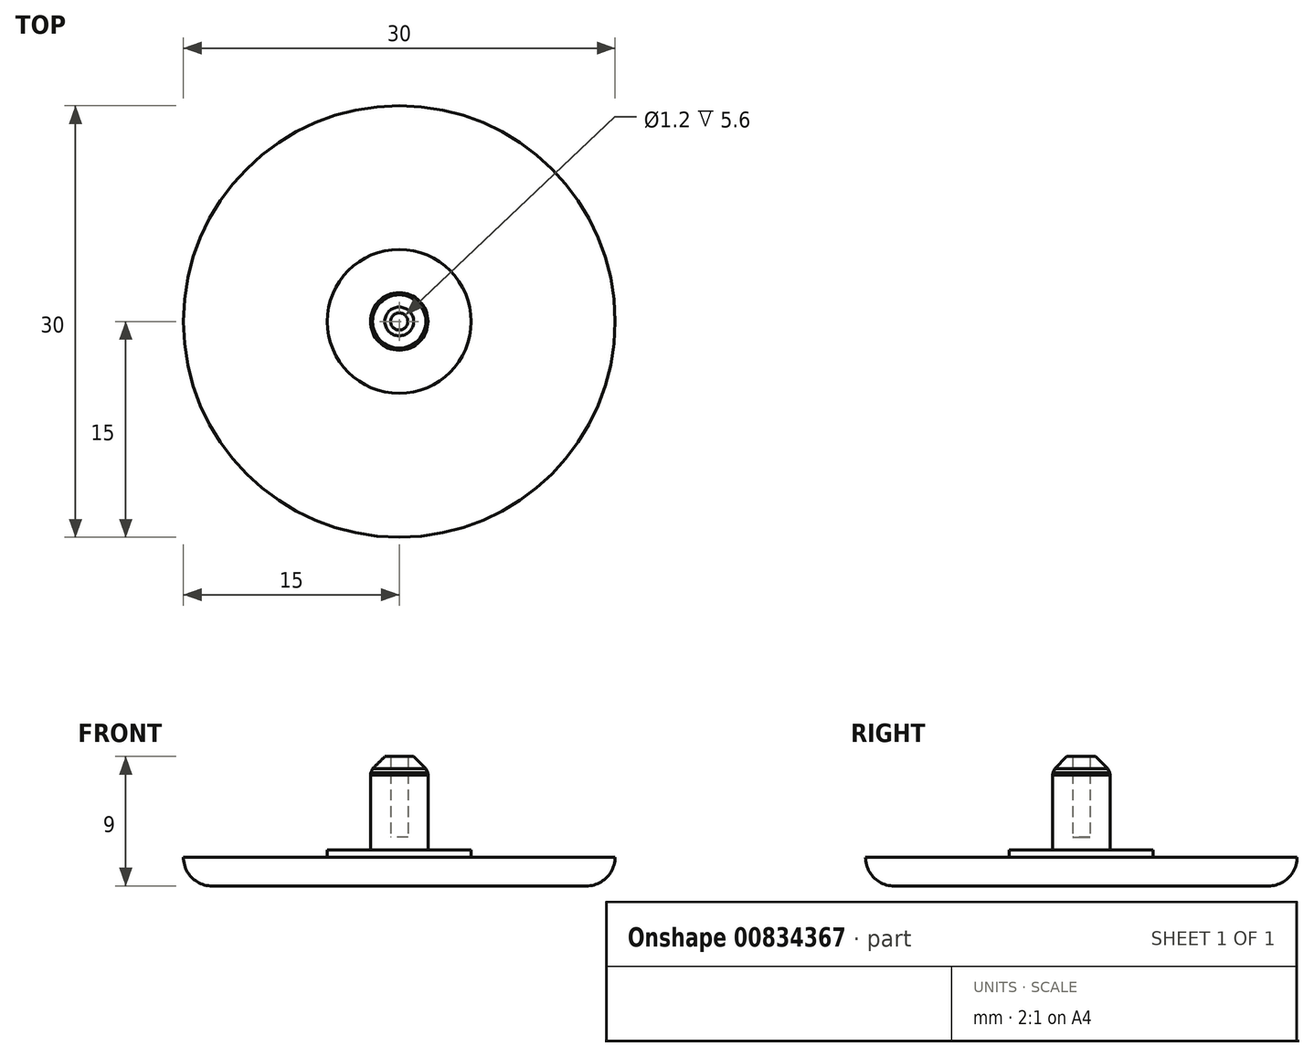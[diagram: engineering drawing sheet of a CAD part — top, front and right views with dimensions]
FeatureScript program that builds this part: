
annotation { "Feature Type Name" : "Feature", "Feature Type Description" : "" }
export const myFeature = defineFeature(function(context is Context, id is Id, definition is map)
    precondition{}
    {
        {
            var Q0;
            Q0=qCreatedBy(makeId("Top.planeOp"),FACE);
            var sketch = newSketch(context, id + "F0", { "sketchPlane" : qUnion([Q0])});
            skCircle(sketch, "E0", {"center": v(0, 0) * mm, "radius": 2 * mm});
            skCircle(sketch, "E1", {"center": v(0, 0) * mm, "radius": 15 * mm});
            skSolve(sketch);
        }
        {
            var Q0;
            Q0=makeQuery(id+"F0.imprint","IMPRINT",FACE,{"disambiguationData":[TD([[makeQuery(id+"F0.imprint","IMPRINT",EDGE,{"derivedFrom":sQuery(id+"F0.wireOp",EDGE,"E0")}),1.0]])]});
            extrude(context, id + "F1", {"entities" : qUnion([Q0]), "depth" : 7 * mm, "offsetDistance" : 25 * mm});
        }
        {
            var Q0;
            Q0=makeQuery(id+"F1.opExtrude","CAP_FACE",FACE,{"disambiguationData":[OSD([sQuery(id+"F0.wireOp",EDGE,"E0")])],"isStart":false});
            shell(context, id + "F2", {"entities" : qUnion([Q0]), "thickness" : 1.4 * mm});
        }
        {
            var Q0;
            Q0=makeQuery(id+"F0.imprint","IMPRINT",FACE,{"disambiguationData":[TD([[makeQuery(id+"F0.imprint","IMPRINT",EDGE,{"derivedFrom":sQuery(id+"F0.wireOp",EDGE,"E0")}),-1.0]])]});
            var Q1;
            Q1=makeQuery(id+"F0.imprint","IMPRINT",FACE,{"disambiguationData":[TD([[makeQuery(id+"F0.imprint","IMPRINT",EDGE,{"derivedFrom":sQuery(id+"F0.wireOp",EDGE,"E0")}),1.0]])]});
            extrude(context, id + "F3", {"entities" : qUnion([Q0, Q1]), "operationType" : NewBodyOperationType.ADD, "oppositeDirection" : true, "depth" : 2 * mm, "offsetDistance" : 25 * mm});
        }
        {
            var Q0;
            Q0=makeQuery(id+"F3.opExtrude","CAP_EDGE",EDGE,{"disambiguationData":[OSD([sQuery(id+"F0.wireOp",EDGE,"E1")])],"isStart":false});
            fillet(context, id + "F4", {"entities" : qUnion([Q0]), "radius" : 2 * mm, "tangentPropagation" : true, "allowEdgeOverflow" : false});
        }
        {
            var Q0;
            Q0=qCreatedBy(makeId("Front.planeOp"),FACE);
            var sketch = newSketch(context, id + "F5", { "sketchPlane" : qUnion([Q0])});
            skLineSegment(sketch, "E2.bottom", {"start": v(0, 0) * mm, "end": v(2.2, 0) * mm});
            skLineSegment(sketch, "E2.top", {"start": v(0, 3.5) * mm, "end": v(2.2, 3.5) * mm});
            skLineSegment(sketch, "E2.left", {"start": v(0, 0) * mm, "end": v(0, 3.5) * mm});
            skLineSegment(sketch, "E2.right", {"start": v(2.2, 0) * mm, "end": v(2.2, 3.5) * mm});
            skCircle(sketch, "E3", {"center": v(2.2, 3.5) * mm, "radius": 0.12 * mm});
            skSolve(sketch);
        }
        {
            var Q0;
            Q0=makeQuery(id+"F1.opExtrude","CAP_EDGE",EDGE,{"disambiguationData":[OSD([sQuery(id+"F0.wireOp",EDGE,"E0")])],"isStart":false});
            chamfer(context, id + "F6", {"entities" : qUnion([Q0]), "width" : 1 * mm, "tangentPropagation" : true});
        }
        {
            var Q0;
            {var subQ0=sQuery(id+"F0.wireOp",EDGE,"E0");Q0=makeQuery(id+"F6.opChamfer","BLEND_EDGE",EDGE,{"blendedFrom":[makeQuery(id+"F1.opExtrude","CAP_EDGE",EDGE,{"disambiguationData":[OSD([subQ0])],"isStart":false}),makeQuery(id+"FCGwViJ1HaKl0xJ_1.boolean.opBoolean","SPLIT",FACE,{"disambiguationData":[TD([makeQuery(id+"F1.opExtrude","CAP_FACE",FACE,{"disambiguationData":[OSD([subQ0])],"isStart":false})])],"derivedFrom":makeQuery(id+"F1.opExtrude","SWEPT_FACE",FACE,{"disambiguationData":[OSD([subQ0])]})})],"blendedInto":[makeQuery(id+"FCGwViJ1HaKl0xJ_1.boolean.opBoolean","SPLIT",FACE,{"disambiguationData":[TD([makeQuery(id+"F1.opExtrude","CAP_FACE",FACE,{"disambiguationData":[OSD([subQ0])],"isStart":false})])],"derivedFrom":makeQuery(id+"F1.opExtrude","SWEPT_FACE",FACE,{"disambiguationData":[OSD([subQ0])]})})]});}
            chamfer(context, id + "F7", {"entities" : qUnion([Q0]), "width" : 0.5 * mm, "tangentPropagation" : true});
        }
        {
            var Q0;
            {var subQ0=sQuery(id+"F0.wireOp",EDGE,"E0");var subQ1=makeQuery(id+"F1.opExtrude","SWEPT_FACE",FACE,{"disambiguationData":[OSD([subQ0])]});Q0=makeQuery(id+"F7.opChamfer","BLEND_EDGE",EDGE,{"blendedFrom":[makeQuery(id+"F6.opChamfer","BLEND_EDGE",EDGE,{"blendedFrom":[makeQuery(id+"F1.opExtrude","CAP_EDGE",EDGE,{"disambiguationData":[OSD([subQ0])],"isStart":false}),subQ1],"blendedInto":[subQ1]}),subQ1],"blendedInto":[subQ1]});}
            chamfer(context, id + "F8", {"entities" : qUnion([Q0]), "width" : 0.35 * mm, "tangentPropagation" : true});
        }
        {
            var Q0;
            Q0=makeQuery(id+"F0.imprint","IMPRINT",FACE,{"disambiguationData":[TD([[makeQuery(id+"F0.imprint","IMPRINT",EDGE,{"derivedFrom":sQuery(id+"F0.wireOp",EDGE,"E0")}),-1.0]])]});
            var sketch = newSketch(context, id + "F9", { "sketchPlane" : qUnion([Q0])});
            skCircle(sketch, "E4", {"center": v(0, 0) * mm, "radius": 5 * mm});
            skSolve(sketch);
        }
        {
            var Q0;
            Q0=makeQuery(id+"F9.imprint","IMPRINT",FACE,{"disambiguationData":[TD([[makeQuery(id+"F9.imprint","IMPRINT",EDGE,{"derivedFrom":sQuery(id+"F9.wireOp",EDGE,"E4")}),1.0]])]});
            extrude(context, id + "F10", {"entities" : qUnion([Q0]), "operationType" : NewBodyOperationType.ADD, "depth" : 0.5 * mm, "offsetDistance" : 25 * mm});
        }
    });
